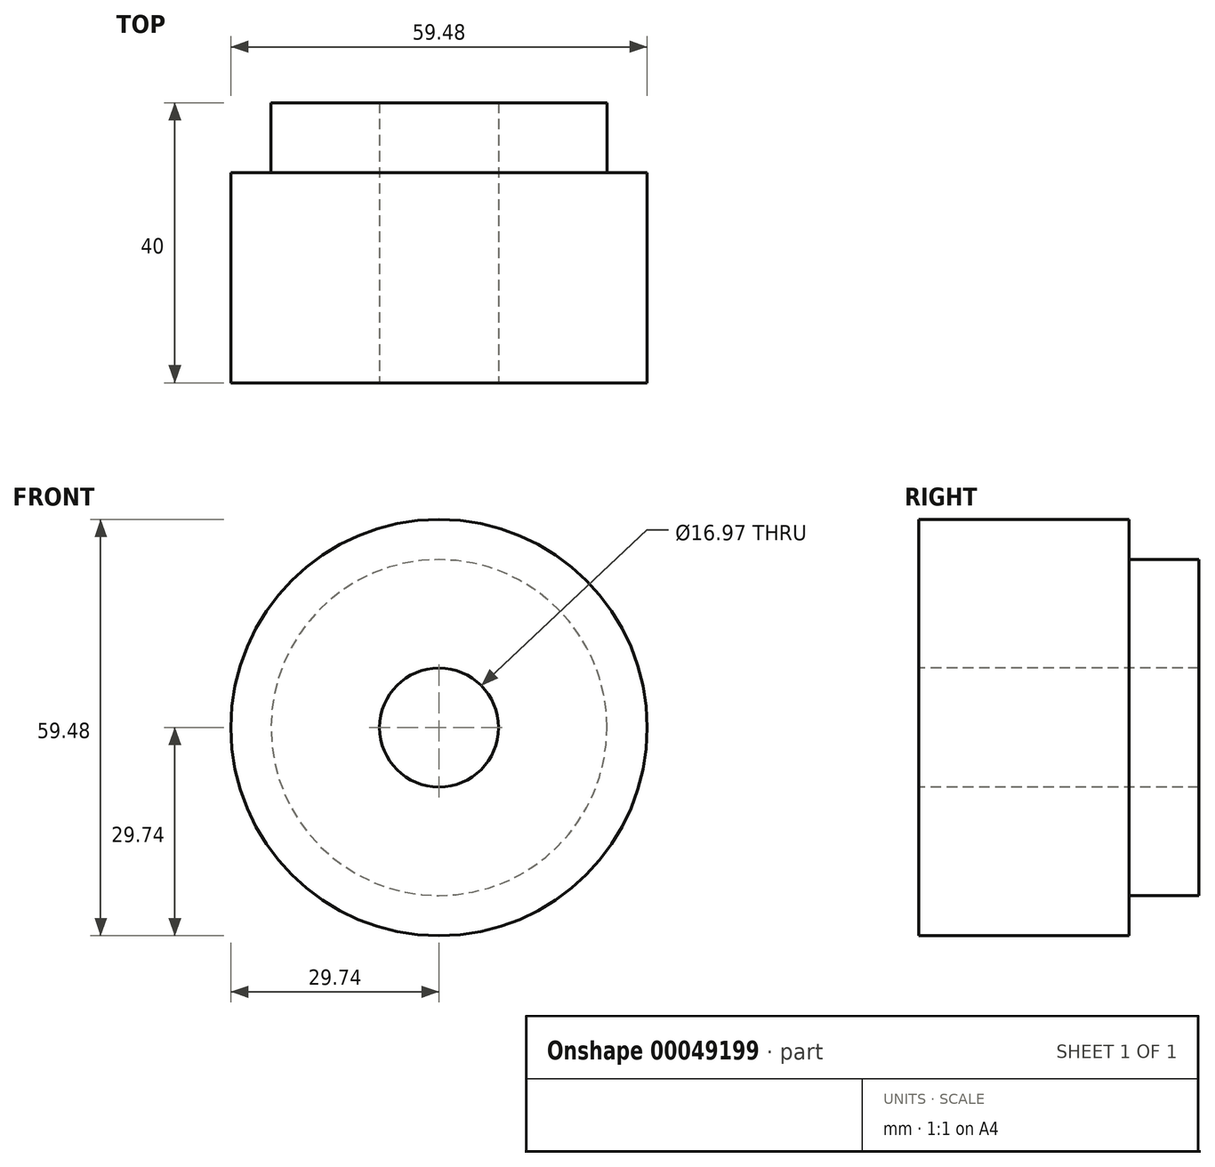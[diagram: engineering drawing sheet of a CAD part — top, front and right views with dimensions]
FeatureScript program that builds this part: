
annotation { "Feature Type Name" : "Feature", "Feature Type Description" : "" }
export const myFeature = defineFeature(function(context is Context, id is Id, definition is map)
    precondition{}
    {
        {
            var Q0;
            Q0=qCreatedBy(makeId("Right.planeOp"),FACE);
            var sketch = newSketch(context, id + "F0", { "sketchPlane" : qUnion([Q0])});
            skLineSegment(sketch, "E0", {"start": v(0, 8.49) * mm, "end": v(0, 29.74) * mm});
            skLineSegment(sketch, "E1", {"start": v(0, 29.74) * mm, "end": v(30, 29.74) * mm});
            skLineSegment(sketch, "E2", {"start": v(30, 29.74) * mm, "end": v(30, 23.99) * mm});
            skLineSegment(sketch, "E3", {"start": v(30, 23.99) * mm, "end": v(40, 23.99) * mm});
            skLineSegment(sketch, "E4", {"start": v(40, 23.99) * mm, "end": v(40, 8.49) * mm});
            skLineSegment(sketch, "E5", {"start": v(40, 8.49) * mm, "end": v(0, 8.49) * mm});
            skLineSegment(sketch, "E6", {"start": v(-35.86, 0) * mm, "end": v(109.32, 0) * mm, "construction": true});
            skSolve(sketch);
        }
        {
            var Q0;
            Q0 = qSketchRegion(id + "F0", true);
            var Q1;
            Q1=sQuery(id+"F0.wireOp",EDGE,"E6");
            revolve(context, id + "F1", {"entities" : qUnion([Q0]), "axis" : qUnion([Q1]), "revolveType" : RevolveType.FULL});
        }
    });
